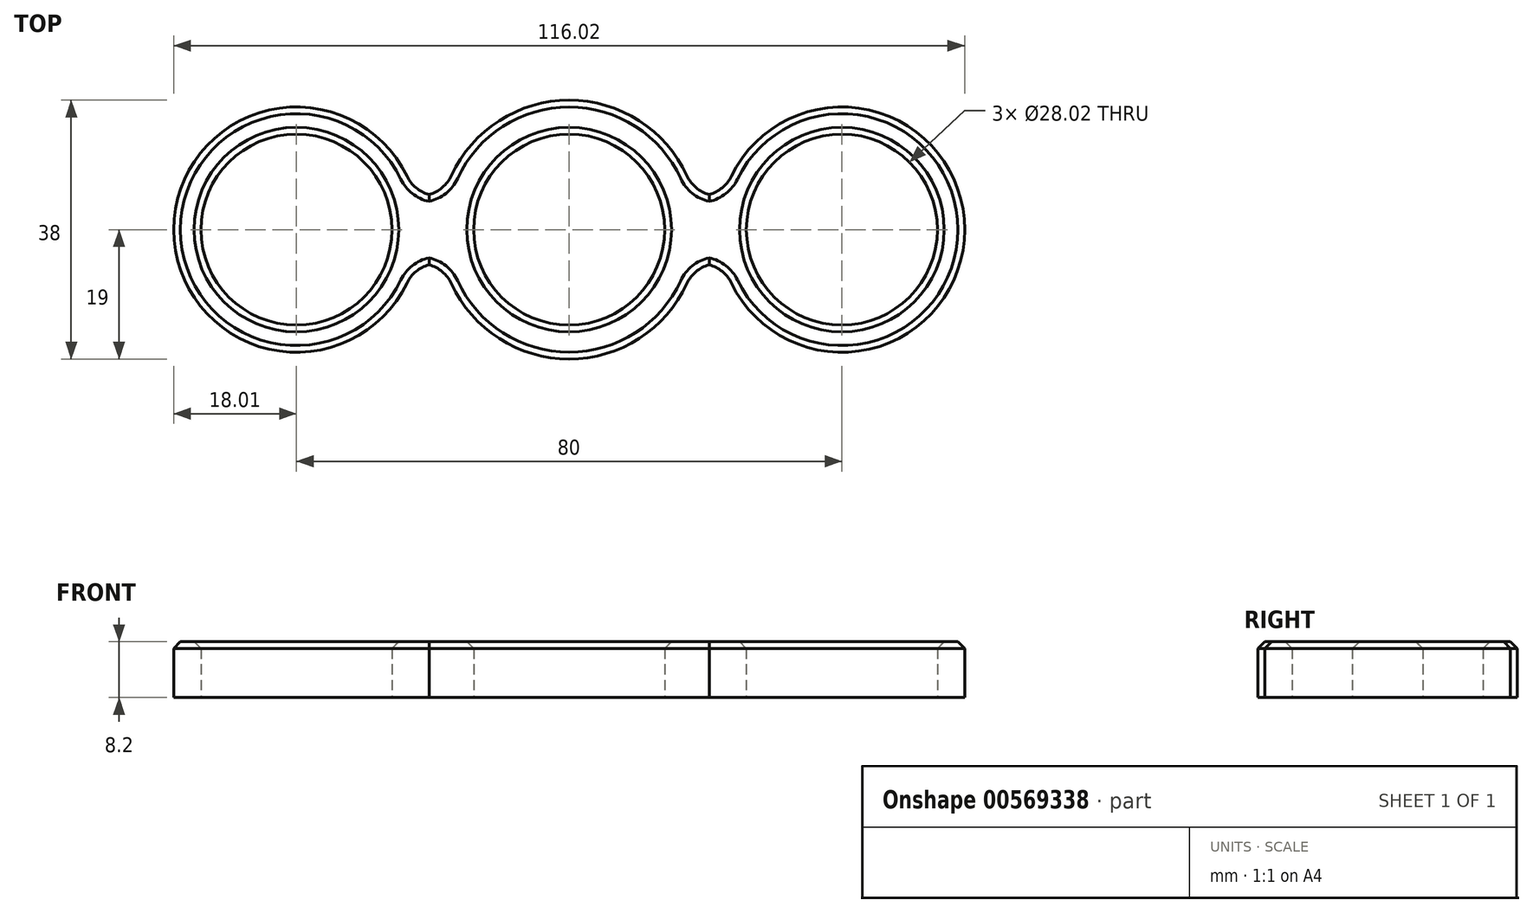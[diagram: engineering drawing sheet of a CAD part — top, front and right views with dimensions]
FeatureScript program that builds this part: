
annotation { "Feature Type Name" : "Feature", "Feature Type Description" : "" }
export const myFeature = defineFeature(function(context is Context, id is Id, definition is map)
    precondition{}
    {
        {
            var Q0;
            Q0=qCreatedBy(makeId("Top.planeOp"),FACE);
            var sketch = newSketch(context, id + "F0", { "sketchPlane" : qUnion([Q0])});
            skArc(sketch, "E0", {"start": v(-18.33, -5) * mm, "mid": v(0, -19) * mm, "end": v(18.33, -5) * mm});
            skCircle(sketch, "E1", {"center": v(0, 0) * mm, "radius": 14 * mm});
            skCircle(sketch, "E2", {"center": v(-40, 0) * mm, "radius": 14 * mm});
            skCircle(sketch, "E3", {"center": v(40, 0) * mm, "radius": 14 * mm});
            skArc(sketch, "E4", {"start": v(-22.7, 5) * mm, "mid": v(-58, 0) * mm, "end": v(-22.7, -5) * mm});
            skArc(sketch, "E5", {"start": v(22.7, -5) * mm, "mid": v(58.01, 0) * mm, "end": v(22.7, 5) * mm});
            skLineSegment(sketch, "E6", {"start": v(-22.7, 5) * mm, "end": v(-18.33, 5) * mm});
            skLineSegment(sketch, "E7", {"start": v(22.7, -5) * mm, "end": v(18.33, -5) * mm});
            skLineSegment(sketch, "E8.trimOffspring", {"start": v(-18.33, -5) * mm, "end": v(-22.7, -5) * mm});
            skLineSegment(sketch, "E9.trimOffspring", {"start": v(18.33, 5) * mm, "end": v(22.7, 5) * mm});
            skArc(sketch, "E10.trimOffspring", {"start": v(18.33, 5) * mm, "mid": v(0, 19) * mm, "end": v(-18.33, 5) * mm});
            skSolve(sketch);
        }
        {
            var Q0;
            Q0=makeQuery(id+"F0.imprint","IMPRINT",FACE,{"disambiguationData":[TD([[makeQuery(id+"F0.imprint","IMPRINT",EDGE,{"derivedFrom":sQuery(id+"F0.wireOp",EDGE,"E0")}),1.0]])]});
            extrude(context, id + "F1", {"entities" : qUnion([Q0]), "depth" : 8.2 * mm, "offsetDistance" : 25 * mm});
        }
        {
            var Q0;
            Q0=makeQuery(id+"F1.opExtrude","SWEPT_EDGE",EDGE,{"disambiguationData":[OSD([sQuery(id+"F0.wireOp",EDGE,"E4"),sQuery(id+"F0.wireOp",EDGE,"E8.trimOffspring")])]});
            var Q1;
            Q1=makeQuery(id+"F1.opExtrude","SWEPT_EDGE",EDGE,{"disambiguationData":[OSD([sQuery(id+"F0.wireOp",EDGE,"E0"),sQuery(id+"F0.wireOp",EDGE,"E8.trimOffspring")])]});
            var Q2;
            Q2=makeQuery(id+"F1.opExtrude","SWEPT_EDGE",EDGE,{"disambiguationData":[OSD([sQuery(id+"F0.wireOp",EDGE,"E0"),sQuery(id+"F0.wireOp",EDGE,"E7")])]});
            var Q3;
            Q3=makeQuery(id+"F1.opExtrude","SWEPT_EDGE",EDGE,{"disambiguationData":[OSD([sQuery(id+"F0.wireOp",EDGE,"E5"),sQuery(id+"F0.wireOp",EDGE,"E7")])]});
            var Q4;
            Q4=makeQuery(id+"F1.opExtrude","SWEPT_EDGE",EDGE,{"disambiguationData":[OSD([sQuery(id+"F0.wireOp",EDGE,"E9.trimOffspring"),sQuery(id+"F0.wireOp",EDGE,"E10.trimOffspring")])]});
            var Q5;
            Q5=makeQuery(id+"F1.opExtrude","SWEPT_EDGE",EDGE,{"disambiguationData":[OSD([sQuery(id+"F0.wireOp",EDGE,"E5"),sQuery(id+"F0.wireOp",EDGE,"E9.trimOffspring")])]});
            var Q6;
            Q6=makeQuery(id+"F1.opExtrude","SWEPT_EDGE",EDGE,{"disambiguationData":[OSD([sQuery(id+"F0.wireOp",EDGE,"E6"),sQuery(id+"F0.wireOp",EDGE,"E10.trimOffspring")])]});
            var Q7;
            Q7=makeQuery(id+"F1.opExtrude","SWEPT_EDGE",EDGE,{"disambiguationData":[OSD([sQuery(id+"F0.wireOp",EDGE,"E4"),sQuery(id+"F0.wireOp",EDGE,"E6")])]});
            fillet(context, id + "F2", {"entities" : qUnion([Q0, Q1, Q2, Q3, Q4, Q5, Q6, Q7]), "radius" : 5 * mm, "tangentPropagation" : true, "allowEdgeOverflow" : false});
        }
        {
            var Q0;
            Q0=makeQuery(id+"F1.opExtrude","CAP_FACE",FACE,{"disambiguationData":[OSD([sQuery(id+"F0.wireOp",EDGE,"E0"),sQuery(id+"F0.wireOp",EDGE,"E1"),sQuery(id+"F0.wireOp",EDGE,"E2"),sQuery(id+"F0.wireOp",EDGE,"E3"),sQuery(id+"F0.wireOp",EDGE,"E4"),sQuery(id+"F0.wireOp",EDGE,"E5"),sQuery(id+"F0.wireOp",EDGE,"E6"),sQuery(id+"F0.wireOp",EDGE,"E7"),sQuery(id+"F0.wireOp",EDGE,"E8.trimOffspring"),sQuery(id+"F0.wireOp",EDGE,"E9.trimOffspring"),sQuery(id+"F0.wireOp",EDGE,"E10.trimOffspring")])],"isStart":false});
            chamfer(context, id + "F3", {"entities" : qUnion([Q0]), "width" : 1 * mm, "tangentPropagation" : true});
        }
    });
